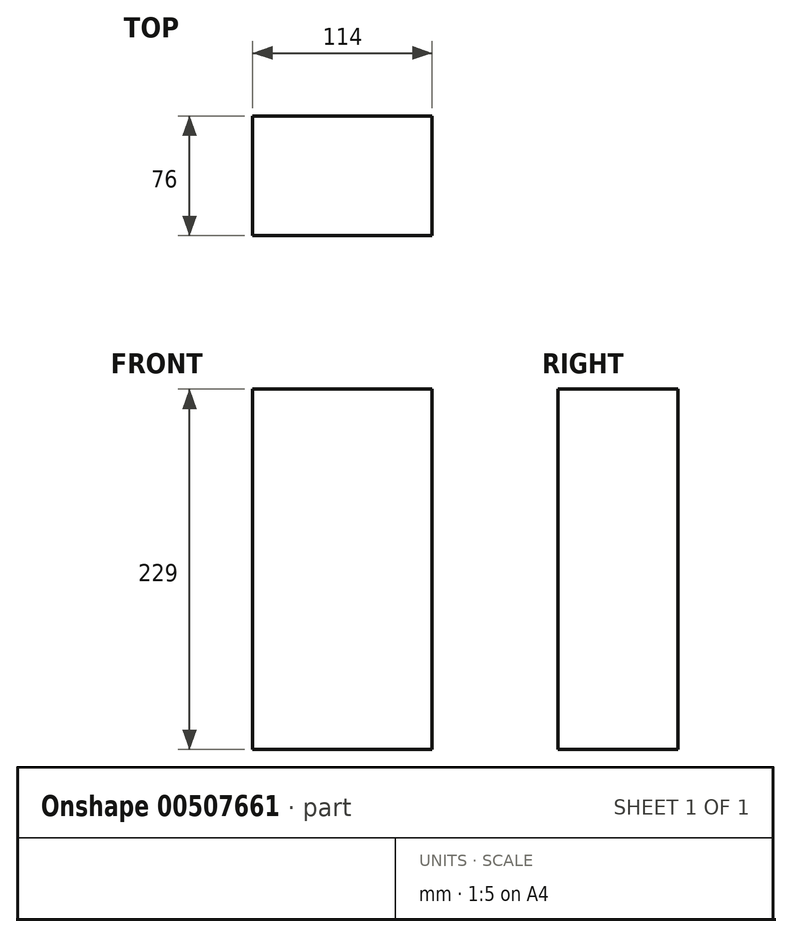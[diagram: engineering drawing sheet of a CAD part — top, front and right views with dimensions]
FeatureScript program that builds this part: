
annotation { "Feature Type Name" : "Feature", "Feature Type Description" : "" }
export const myFeature = defineFeature(function(context is Context, id is Id, definition is map)
    precondition{}
    {
        {
            var Q0;
            Q0=qCreatedBy(makeId("Top.planeOp"),FACE);
            var sketch = newSketch(context, id + "F0", { "sketchPlane" : qUnion([Q0])});
            skLineSegment(sketch, "E0.bottom", {"start": v(0, 0) * mm, "end": v(114, 0) * mm});
            skLineSegment(sketch, "E0.top", {"start": v(0, 76) * mm, "end": v(114, 76) * mm});
            skLineSegment(sketch, "E0.left", {"start": v(0, 0) * mm, "end": v(0, 76) * mm});
            skLineSegment(sketch, "E0.right", {"start": v(114, 0) * mm, "end": v(114, 76) * mm});
            skSolve(sketch);
        }
        {
            var Q0;
            Q0 = qSketchRegion(id + "F0", true);
            extrude(context, id + "F1", {"entities" : qUnion([Q0]), "depth" : 229 * mm});
        }
    });
